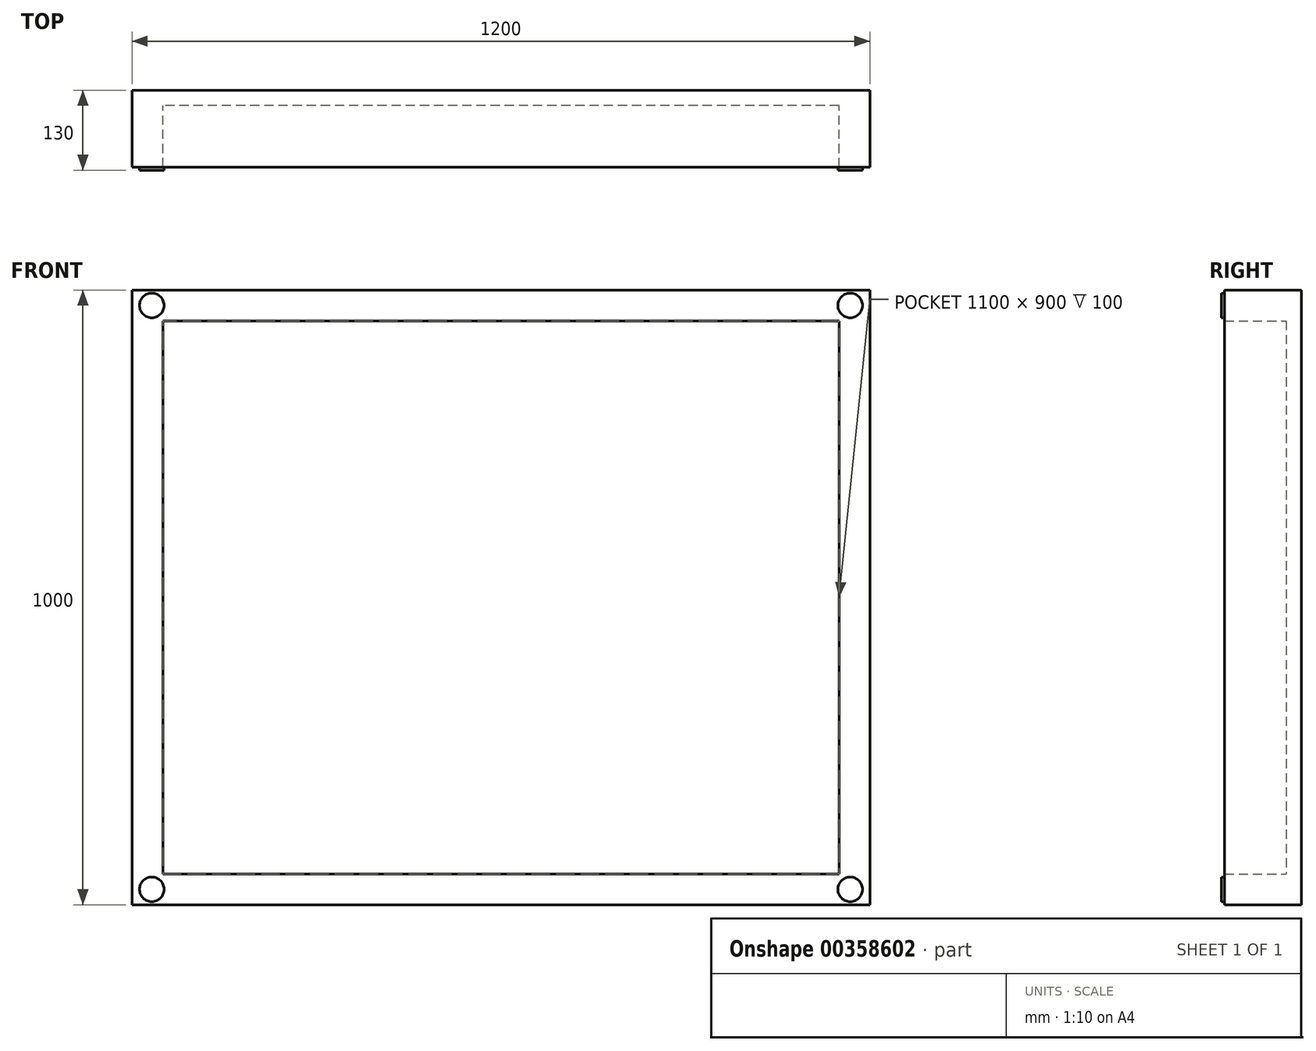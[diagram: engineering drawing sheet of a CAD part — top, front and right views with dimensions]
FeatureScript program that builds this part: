
annotation { "Feature Type Name" : "Feature", "Feature Type Description" : "" }
export const myFeature = defineFeature(function(context is Context, id is Id, definition is map)
    precondition{}
    {
        {
            var Q0;
            Q0=qCreatedBy(makeId("Front.planeOp"),FACE);
            var sketch = newSketch(context, id + "F0", { "sketchPlane" : qUnion([Q0])});
            skLineSegment(sketch, "E0.bottom", {"start": v(600, -500) * mm, "end": v(-600, -500) * mm});
            skLineSegment(sketch, "E0.top", {"start": v(600, 500) * mm, "end": v(-600, 500) * mm});
            skLineSegment(sketch, "E0.left", {"start": v(600, -500) * mm, "end": v(600, 500) * mm});
            skLineSegment(sketch, "E0.right", {"start": v(-600, -500) * mm, "end": v(-600, 500) * mm});
            skPoint(sketch, "E0.middle", {"position": v(0, 0) * mm});
            skSolve(sketch);
        }
        {
            var Q0;
            Q0 = qSketchRegion(id + "F0", true);
            extrude(context, id + "F1", {"entities" : qUnion([Q0]), "depth" : 25 * mm});
        }
        {
            var Q0;
            Q0=makeQuery(id+"F1.opExtrude","SWEPT_FACE",FACE,{"disambiguationData":[OSD([sQuery(id+"F0.wireOp",EDGE,"E0.top")])]});
            var sketch = newSketch(context, id + "F2", { "sketchPlane" : qUnion([Q0])});
            skLineSegment(sketch, "E1.bottom", {"start": v(-600, -25) * mm, "end": v(600, -25) * mm});
            skLineSegment(sketch, "E1.top", {"start": v(-600, -125) * mm, "end": v(600, -125) * mm});
            skLineSegment(sketch, "E1.left", {"start": v(-600, -25) * mm, "end": v(-600, -125) * mm});
            skLineSegment(sketch, "E1.right", {"start": v(600, -25) * mm, "end": v(600, -125) * mm});
            skSolve(sketch);
        }
        {
            var Q0;
            Q0 = qSketchRegion(id + "F2", true);
            extrude(context, id + "F3", {"entities" : qUnion([Q0]), "operationType" : NewBodyOperationType.ADD, "oppositeDirection" : true, "depth" : 50 * mm});
        }
        {
            var Q0;
            Q0=makeQuery(id+"F1.opExtrude","SWEPT_FACE",FACE,{"disambiguationData":[OSD([sQuery(id+"F0.wireOp",EDGE,"E0.bottom")])]});
            var sketch = newSketch(context, id + "F4", { "sketchPlane" : qUnion([Q0])});
            skLineSegment(sketch, "E2.bottom", {"start": v(-600, 25) * mm, "end": v(600, 25) * mm});
            skLineSegment(sketch, "E2.top", {"start": v(-600, 125) * mm, "end": v(600, 125) * mm});
            skLineSegment(sketch, "E2.left", {"start": v(-600, 25) * mm, "end": v(-600, 125) * mm});
            skLineSegment(sketch, "E2.right", {"start": v(600, 25) * mm, "end": v(600, 125) * mm});
            skSolve(sketch);
        }
        {
            var Q0;
            Q0 = qSketchRegion(id + "F4", true);
            extrude(context, id + "F5", {"entities" : qUnion([Q0]), "operationType" : NewBodyOperationType.ADD, "oppositeDirection" : true, "depth" : 50 * mm});
        }
        {
            var Q0;
            Q0=makeQuery(id+"F3.opExtrude","SWEPT_FACE",FACE,{"disambiguationData":[OSD([sQuery(id+"F2.wireOp",EDGE,"E1.top")])]});
            var sketch = newSketch(context, id + "F6", { "sketchPlane" : qUnion([Q0])});
            skCircle(sketch, "E3", {"center": v(-568, 475) * mm, "radius": 20 * mm});
            skPoint(sketch, "E3.centerSnap0", {"position": v(-600, 475) * mm});
            skLineSegment(sketch, "E4", {"start": v(-376.66, 0) * mm, "end": v(379.82, 0) * mm, "construction": true});
            skLineSegment(sketch, "E5", {"start": v(0, 366.12) * mm, "end": v(0, -374.45) * mm, "construction": true});
            skPoint(sketch, "E5.endSnap0", {"position": v(0, 500) * mm});
            skCircle(sketch, "E6.MirrorC", {"center": v(568, 475) * mm, "radius": 20 * mm});
            skCircle(sketch, "E7.MirrorC", {"center": v(-568, -475) * mm, "radius": 20 * mm});
            skCircle(sketch, "E8.MirrorC", {"center": v(568, -475) * mm, "radius": 20 * mm});
            skSolve(sketch);
        }
        {
            var Q0;
            Q0 = qSketchRegion(id + "F6", true);
            extrude(context, id + "F7", {"entities" : qUnion([Q0]), "operationType" : NewBodyOperationType.ADD, "depth" : 5 * mm});
        }
        {
            var Q0;
            Q0=makeQuery(id+"F1.opExtrude","CAP_FACE",FACE,{"disambiguationData":[OSD([sQuery(id+"F0.wireOp",EDGE,"E0.bottom"),sQuery(id+"F0.wireOp",EDGE,"E0.top"),sQuery(id+"F0.wireOp",EDGE,"E0.left"),sQuery(id+"F0.wireOp",EDGE,"E0.right")])],"isStart":false});
            var sketch = newSketch(context, id + "F8", { "sketchPlane" : qUnion([Q0])});
            skLineSegment(sketch, "E9.bottom", {"start": v(600, 450) * mm, "end": v(550, 450) * mm});
            skLineSegment(sketch, "E9.top", {"start": v(600, -450) * mm, "end": v(550, -450) * mm});
            skLineSegment(sketch, "E9.left", {"start": v(600, 450) * mm, "end": v(600, -450) * mm});
            skLineSegment(sketch, "E9.right", {"start": v(550, 450) * mm, "end": v(550, -450) * mm});
            skSolve(sketch);
        }
        {
            var Q0;
            Q0 = qSketchRegion(id + "F8", true);
            extrude(context, id + "F9", {"entities" : qUnion([Q0]), "operationType" : NewBodyOperationType.ADD, "depth" : 100 * mm});
        }
        {
            var Q0;
            Q0=makeQuery(id+"F1.opExtrude","CAP_FACE",FACE,{"disambiguationData":[OSD([sQuery(id+"F0.wireOp",EDGE,"E0.bottom"),sQuery(id+"F0.wireOp",EDGE,"E0.top"),sQuery(id+"F0.wireOp",EDGE,"E0.left"),sQuery(id+"F0.wireOp",EDGE,"E0.right")])],"isStart":false});
            var sketch = newSketch(context, id + "F10", { "sketchPlane" : qUnion([Q0])});
            skLineSegment(sketch, "E10.bottom", {"start": v(-600, 450) * mm, "end": v(-550, 450) * mm});
            skLineSegment(sketch, "E10.top", {"start": v(-600, -450) * mm, "end": v(-550, -450) * mm});
            skLineSegment(sketch, "E10.left", {"start": v(-600, 450) * mm, "end": v(-600, -450) * mm});
            skLineSegment(sketch, "E10.right", {"start": v(-550, 450) * mm, "end": v(-550, -450) * mm});
            skSolve(sketch);
        }
        {
            var Q0;
            Q0 = qSketchRegion(id + "F10", true);
            extrude(context, id + "F11", {"entities" : qUnion([Q0]), "operationType" : NewBodyOperationType.ADD, "depth" : 100 * mm});
        }
    });
